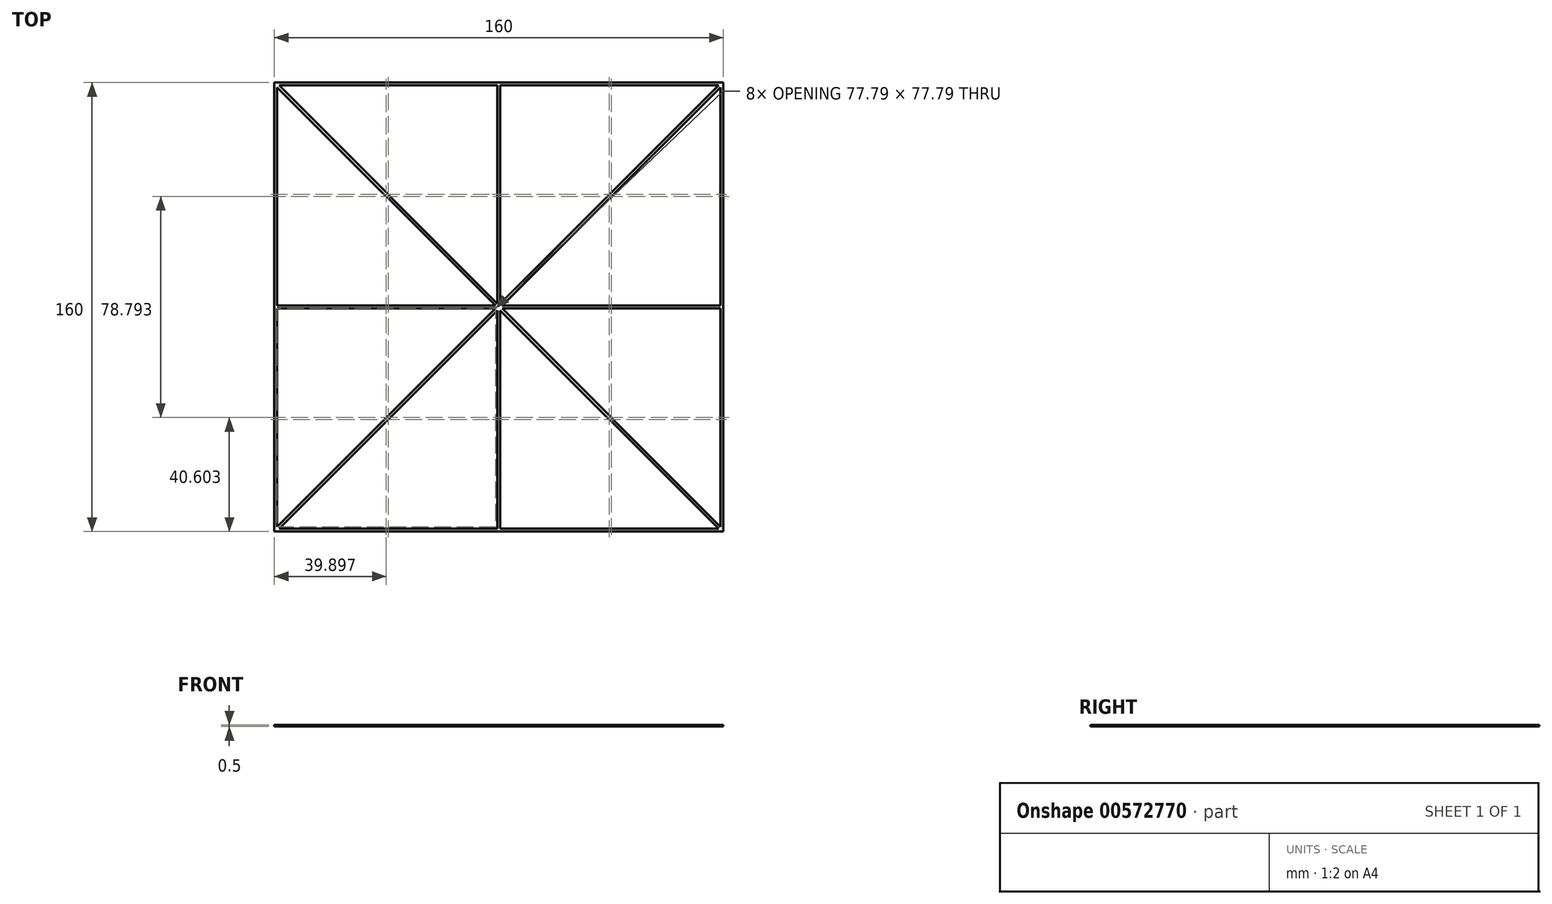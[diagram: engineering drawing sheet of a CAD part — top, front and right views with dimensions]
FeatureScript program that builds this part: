
annotation { "Feature Type Name" : "Feature", "Feature Type Description" : "" }
export const myFeature = defineFeature(function(context is Context, id is Id, definition is map)
    precondition{}
    {
        {
            var Q0;
            Q0=qCreatedBy(makeId("Top.planeOp"),FACE);
            var sketch = newSketch(context, id + "F0", { "sketchPlane" : qUnion([Q0])});
            skLineSegment(sketch, "E0.bottom", {"start": v(0, 0) * mm, "end": v(160, 0) * mm});
            skLineSegment(sketch, "E0.top", {"start": v(0, -160) * mm, "end": v(160, -160) * mm});
            skLineSegment(sketch, "E0.left", {"start": v(0, 0) * mm, "end": v(0, -160) * mm});
            skLineSegment(sketch, "E0.right", {"start": v(160, 0) * mm, "end": v(160, -160) * mm});
            skLineSegment(sketch, "E1", {"start": v(0, 0) * mm, "end": v(0, -1) * mm});
            skLineSegment(sketch, "E2", {"start": v(0, -1) * mm, "end": v(1, -1) * mm});
            skLineSegment(sketch, "E3.bottom", {"start": v(1, -1) * mm, "end": v(159, -1) * mm});
            skLineSegment(sketch, "E3.top", {"start": v(1, -159) * mm, "end": v(159, -159) * mm});
            skLineSegment(sketch, "E3.left", {"start": v(1, -1) * mm, "end": v(1, -159) * mm});
            skLineSegment(sketch, "E3.right", {"start": v(159, -1) * mm, "end": v(159, -159) * mm});
            skLineSegment(sketch, "E4", {"start": v(1, -80) * mm, "end": v(1, -79.5) * mm});
            skLineSegment(sketch, "E5", {"start": v(1, -79.5) * mm, "end": v(159, -79.5) * mm});
            skLineSegment(sketch, "E6", {"start": v(159, -79.5) * mm, "end": v(159, -80.5) * mm});
            skLineSegment(sketch, "E7", {"start": v(159, -80.5) * mm, "end": v(1, -80.5) * mm});
            skLineSegment(sketch, "E8", {"start": v(1, -80.5) * mm, "end": v(1, -79.5) * mm});
            skLineSegment(sketch, "E9", {"start": v(80, -159) * mm, "end": v(80.5, -159) * mm});
            skLineSegment(sketch, "E10", {"start": v(80.5, -159) * mm, "end": v(80.5, -1) * mm});
            skLineSegment(sketch, "E11", {"start": v(80.5, -1) * mm, "end": v(80, -1) * mm});
            skLineSegment(sketch, "E12", {"start": v(80, -1) * mm, "end": v(80, -159) * mm});
            skLineSegment(sketch, "E13", {"start": v(1, -159) * mm, "end": v(159, -1) * mm});
            skLineSegment(sketch, "E14", {"start": v(150.15, -9.85) * mm, "end": v(150.5, -10.2) * mm});
            skLineSegment(sketch, "E15", {"start": v(150.5, -10.2) * mm, "end": v(149.8, -9.5) * mm});
            skLineSegment(sketch, "E16", {"start": v(149.8, -9.5) * mm, "end": v(158.3, -1) * mm});
            skLineSegment(sketch, "E17", {"start": v(158.3, -1) * mm, "end": v(1, -158.3) * mm});
            skLineSegment(sketch, "E18", {"start": v(1, -158.3) * mm, "end": v(1.7, -159) * mm});
            skLineSegment(sketch, "E19", {"start": v(1.7, -159) * mm, "end": v(159, -1.7) * mm});
            skLineSegment(sketch, "E20", {"start": v(1, -1) * mm, "end": v(159, -159) * mm});
            skLineSegment(sketch, "E21", {"start": v(146.24, -146.24) * mm, "end": v(146.6, -145.89) * mm});
            skLineSegment(sketch, "E22", {"start": v(146.6, -145.89) * mm, "end": v(145.89, -146.6) * mm});
            skLineSegment(sketch, "E23", {"start": v(145.89, -146.6) * mm, "end": v(158.3, -159) * mm});
            skLineSegment(sketch, "E24", {"start": v(158.3, -159) * mm, "end": v(159, -158.3) * mm});
            skLineSegment(sketch, "E25", {"start": v(159, -158.3) * mm, "end": v(1.7, -1) * mm});
            skLineSegment(sketch, "E26", {"start": v(1.7, -1) * mm, "end": v(1, -1.7) * mm});
            skLineSegment(sketch, "E27", {"start": v(1, -1.7) * mm, "end": v(158.3, -159) * mm});
            skLineSegment(sketch, "E28", {"start": v(80, -1) * mm, "end": v(79.5, -1) * mm});
            skLineSegment(sketch, "E29", {"start": v(79.5, -1) * mm, "end": v(79.5, -159) * mm});
            skSolve(sketch);
        }
        {
            var Q0;
            {var subQ0=sQuery(id+"F0.wireOp",EDGE,"E12");var subQ1=sQuery(id+"F0.wireOp",EDGE,"E7");var subQ2=makeQuery(id+"F0.imprint","INTERSECT",VERTEX,{"derivedFrom":[subQ1,subQ0]});Q0=makeQuery(id+"F0.imprint","IMPRINT",FACE,{"disambiguationData":[TD([[makeQuery(id+"F0.imprint","IMPRINT",EDGE,{"disambiguationData":[TD([[subQ2,1.0]])],"derivedFrom":subQ1}),1.0]])]});}
            var Q1;
            {var subQ0=sQuery(id+"F0.wireOp",EDGE,"E12");var subQ1=sQuery(id+"F0.wireOp",EDGE,"E7");var subQ2=makeQuery(id+"F0.imprint","INTERSECT",VERTEX,{"derivedFrom":[subQ1,subQ0]});Q1=makeQuery(id+"F0.imprint","IMPRINT",FACE,{"disambiguationData":[TD([[makeQuery(id+"F0.imprint","IMPRINT",EDGE,{"disambiguationData":[TD([[subQ2,-1.0]])],"derivedFrom":subQ1}),1.0]])]});}
            var Q2;
            {var subQ31=sQuery(id+"F0.wireOp",EDGE,"E0.bottom");Q2=makeQuery(id+"F0.imprint","IMPRINT",FACE,{"disambiguationData":[TD([[makeQuery(id+"F0.imprint","IMPRINT",EDGE,{"derivedFrom":subQ31}),-1.0]])]});}
            var Q3;
            {var subQ0=sQuery(id+"F0.wireOp",EDGE,"E20");var subQ3=sQuery(id+"F0.wireOp",EDGE,"E26");var subQ5=makeQuery(id+"F0.imprint","INTERSECT",VERTEX,{"derivedFrom":[subQ0,subQ3]});Q3=makeQuery(id+"F0.imprint","IMPRINT",FACE,{"disambiguationData":[TD([[makeQuery(id+"F0.imprint","IMPRINT",EDGE,{"disambiguationData":[TD([[subQ5,1.0]])],"derivedFrom":subQ0}),1.0]])]});}
            var Q4;
            {var subQ0=sQuery(id+"F0.wireOp",EDGE,"E12");var subQ1=sQuery(id+"F0.wireOp",EDGE,"E3.bottom");var subQ2=makeQuery(id+"F0.imprint","INTERSECT",VERTEX,{"derivedFrom":[subQ1,subQ0]});Q4=makeQuery(id+"F0.imprint","IMPRINT",FACE,{"disambiguationData":[TD([[makeQuery(id+"F0.imprint","IMPRINT",EDGE,{"disambiguationData":[TD([[subQ2,-1.0]])],"derivedFrom":subQ1}),-1.0]])]});}
            var Q5;
            {var subQ1=sQuery(id+"F0.wireOp",EDGE,"E5");var subQ6=sQuery(id+"F0.wireOp",EDGE,"E3.right");var subQ9=makeQuery(id+"F0.imprint","INTERSECT",VERTEX,{"derivedFrom":[subQ6,subQ1]});Q5=makeQuery(id+"F0.imprint","IMPRINT",FACE,{"disambiguationData":[TD([[makeQuery(id+"F0.imprint","IMPRINT",EDGE,{"disambiguationData":[TD([[subQ9,-1.0]])],"derivedFrom":subQ6}),-1.0]])]});}
            var Q6;
            {var subQ0=sQuery(id+"F0.wireOp",EDGE,"E18");var subQ3=sQuery(id+"F0.wireOp",EDGE,"E13");var subQ5=makeQuery(id+"F0.imprint","INTERSECT",VERTEX,{"derivedFrom":[subQ3,subQ0]});Q6=makeQuery(id+"F0.imprint","IMPRINT",FACE,{"disambiguationData":[TD([[makeQuery(id+"F0.imprint","IMPRINT",EDGE,{"disambiguationData":[TD([[subQ5,1.0]])],"derivedFrom":subQ3}),-1.0]])]});}
            var Q7;
            {var subQ1=sQuery(id+"F0.wireOp",EDGE,"E3.left");var subQ5=makeQuery(id+"F0.imprint","IMPRINT",VERTEX,{"derivedFrom":subQ1});Q7=makeQuery(id+"F0.imprint","IMPRINT",FACE,{"disambiguationData":[TD([[makeQuery(id+"F0.imprint","IMPRINT",EDGE,{"disambiguationData":[TD([[subQ5,-1.0]])],"derivedFrom":subQ1}),1.0]])]});}
            var Q8;
            {var subQ0=sQuery(id+"F0.wireOp",EDGE,"E25");var subQ1=sQuery(id+"F0.wireOp",EDGE,"E5");var subQ2=makeQuery(id+"F0.imprint","INTERSECT",VERTEX,{"derivedFrom":[subQ1,subQ0]});Q8=makeQuery(id+"F0.imprint","IMPRINT",FACE,{"disambiguationData":[TD([[makeQuery(id+"F0.imprint","IMPRINT",EDGE,{"disambiguationData":[TD([[subQ2,1.0]])],"derivedFrom":subQ0}),-1.0]])]});}
            var Q9;
            {var subQ0=sQuery(id+"F0.wireOp",EDGE,"E12");var subQ1=sQuery(id+"F0.wireOp",EDGE,"E7");var subQ2=makeQuery(id+"F0.imprint","INTERSECT",VERTEX,{"derivedFrom":[subQ1,subQ0]});Q9=makeQuery(id+"F0.imprint","IMPRINT",FACE,{"disambiguationData":[TD([[makeQuery(id+"F0.imprint","IMPRINT",EDGE,{"disambiguationData":[TD([[subQ2,-1.0]])],"derivedFrom":subQ1}),-1.0]])]});}
            var Q10;
            {var subQ0=sQuery(id+"F0.wireOp",EDGE,"E25");var subQ1=sQuery(id+"F0.wireOp",EDGE,"E5");var subQ2=makeQuery(id+"F0.imprint","INTERSECT",VERTEX,{"derivedFrom":[subQ1,subQ0]});Q10=makeQuery(id+"F0.imprint","IMPRINT",FACE,{"disambiguationData":[TD([[makeQuery(id+"F0.imprint","IMPRINT",EDGE,{"disambiguationData":[TD([[subQ2,1.0]])],"derivedFrom":subQ1}),-1.0]])]});}
            var Q11;
            {var subQ0=sQuery(id+"F0.wireOp",EDGE,"E25");var subQ1=sQuery(id+"F0.wireOp",EDGE,"E5");var subQ2=makeQuery(id+"F0.imprint","INTERSECT",VERTEX,{"derivedFrom":[subQ1,subQ0]});Q11=makeQuery(id+"F0.imprint","IMPRINT",FACE,{"disambiguationData":[TD([[makeQuery(id+"F0.imprint","IMPRINT",EDGE,{"disambiguationData":[TD([[subQ2,1.0]])],"derivedFrom":subQ1}),1.0]])]});}
            var Q12;
            {var subQ0=sQuery(id+"F0.wireOp",EDGE,"E12");var subQ1=sQuery(id+"F0.wireOp",EDGE,"E5");var subQ2=makeQuery(id+"F0.imprint","INTERSECT",VERTEX,{"derivedFrom":[subQ1,subQ0]});Q12=makeQuery(id+"F0.imprint","IMPRINT",FACE,{"disambiguationData":[TD([[makeQuery(id+"F0.imprint","IMPRINT",EDGE,{"disambiguationData":[TD([[subQ2,1.0]])],"derivedFrom":subQ1}),1.0]])]});}
            var Q13;
            {var subQ0=sQuery(id+"F0.wireOp",EDGE,"E19");var subQ1=sQuery(id+"F0.wireOp",EDGE,"E5");var subQ2=makeQuery(id+"F0.imprint","INTERSECT",VERTEX,{"derivedFrom":[subQ1,subQ0]});Q13=makeQuery(id+"F0.imprint","IMPRINT",FACE,{"disambiguationData":[TD([[makeQuery(id+"F0.imprint","IMPRINT",EDGE,{"disambiguationData":[TD([[subQ2,1.0]])],"derivedFrom":subQ0}),1.0]])]});}
            var Q14;
            {var subQ0=sQuery(id+"F0.wireOp",EDGE,"E19");var subQ1=sQuery(id+"F0.wireOp",EDGE,"E10");var subQ2=makeQuery(id+"F0.imprint","INTERSECT",VERTEX,{"derivedFrom":[subQ1,subQ0]});Q14=makeQuery(id+"F0.imprint","IMPRINT",FACE,{"disambiguationData":[TD([[makeQuery(id+"F0.imprint","IMPRINT",EDGE,{"disambiguationData":[TD([[subQ2,-1.0]])],"derivedFrom":subQ1}),-1.0]])]});}
            var Q15;
            {var subQ0=sQuery(id+"F0.wireOp",EDGE,"E13");var subQ3=sQuery(id+"F0.wireOp",EDGE,"E27");var subQ5=makeQuery(id+"F0.imprint","INTERSECT",VERTEX,{"derivedFrom":[subQ0,subQ3]});Q15=makeQuery(id+"F0.imprint","IMPRINT",FACE,{"disambiguationData":[TD([[makeQuery(id+"F0.imprint","IMPRINT",EDGE,{"disambiguationData":[TD([[subQ5,-1.0]])],"derivedFrom":subQ3}),-1.0]])]});}
            var Q16;
            {var subQ0=sQuery(id+"F0.wireOp",EDGE,"E19");var subQ1=sQuery(id+"F0.wireOp",EDGE,"E7");var subQ2=makeQuery(id+"F0.imprint","INTERSECT",VERTEX,{"derivedFrom":[subQ1,subQ0]});Q16=makeQuery(id+"F0.imprint","IMPRINT",FACE,{"disambiguationData":[TD([[makeQuery(id+"F0.imprint","IMPRINT",EDGE,{"disambiguationData":[TD([[subQ2,-1.0]])],"derivedFrom":subQ0}),-1.0]])]});}
            var Q17;
            {var subQ0=sQuery(id+"F0.wireOp",EDGE,"E19");var subQ1=sQuery(id+"F0.wireOp",EDGE,"E7");var subQ2=makeQuery(id+"F0.imprint","INTERSECT",VERTEX,{"derivedFrom":[subQ1,subQ0]});Q17=makeQuery(id+"F0.imprint","IMPRINT",FACE,{"disambiguationData":[TD([[makeQuery(id+"F0.imprint","IMPRINT",EDGE,{"disambiguationData":[TD([[subQ2,1.0]])],"derivedFrom":subQ1}),1.0]])]});}
            var Q18;
            {var subQ0=sQuery(id+"F0.wireOp",EDGE,"E12");var subQ1=sQuery(id+"F0.wireOp",EDGE,"E3.bottom");var subQ2=makeQuery(id+"F0.imprint","INTERSECT",VERTEX,{"derivedFrom":[subQ1,subQ0]});Q18=makeQuery(id+"F0.imprint","IMPRINT",FACE,{"disambiguationData":[TD([[makeQuery(id+"F0.imprint","IMPRINT",EDGE,{"disambiguationData":[TD([[subQ2,1.0]])],"derivedFrom":subQ1}),-1.0]])]});}
            var Q19;
            {var subQ0=sQuery(id+"F0.wireOp",EDGE,"E26");var subQ1=sQuery(id+"F0.wireOp",EDGE,"E20");var subQ2=makeQuery(id+"F0.imprint","INTERSECT",VERTEX,{"derivedFrom":[subQ1,subQ0]});Q19=makeQuery(id+"F0.imprint","IMPRINT",FACE,{"disambiguationData":[TD([[makeQuery(id+"F0.imprint","IMPRINT",EDGE,{"disambiguationData":[TD([[subQ2,-1.0]])],"derivedFrom":subQ1}),1.0]])]});}
            var Q20;
            {var subQ0=sQuery(id+"F0.wireOp",EDGE,"E27");var subQ1=sQuery(id+"F0.wireOp",EDGE,"E5");var subQ2=makeQuery(id+"F0.imprint","INTERSECT",VERTEX,{"derivedFrom":[subQ1,subQ0]});Q20=makeQuery(id+"F0.imprint","IMPRINT",FACE,{"disambiguationData":[TD([[makeQuery(id+"F0.imprint","IMPRINT",EDGE,{"disambiguationData":[TD([[subQ2,-1.0]])],"derivedFrom":subQ1}),1.0]])]});}
            var Q21;
            {var subQ5=sQuery(id+"F0.wireOp",EDGE,"E15");Q21=makeQuery(id+"F0.imprint","IMPRINT",FACE,{"disambiguationData":[TD([[makeQuery(id+"F0.imprint","IMPRINT",EDGE,{"derivedFrom":subQ5}),1.0]])]});}
            var Q22;
            {var subQ5=sQuery(id+"F0.wireOp",EDGE,"E21");Q22=makeQuery(id+"F0.imprint","IMPRINT",FACE,{"disambiguationData":[TD([[makeQuery(id+"F0.imprint","IMPRINT",EDGE,{"derivedFrom":subQ5}),1.0]])]});}
            var Q23;
            {var subQ5=sQuery(id+"F0.wireOp",EDGE,"E22");Q23=makeQuery(id+"F0.imprint","IMPRINT",FACE,{"disambiguationData":[TD([[makeQuery(id+"F0.imprint","IMPRINT",EDGE,{"derivedFrom":subQ5}),-1.0]])]});}
            var Q24;
            {var subQ0=sQuery(id+"F0.wireOp",EDGE,"E10");var subQ1=sQuery(id+"F0.wireOp",EDGE,"E3.top");var subQ2=makeQuery(id+"F0.imprint","INTERSECT",VERTEX,{"derivedFrom":[subQ1,subQ0]});Q24=makeQuery(id+"F0.imprint","IMPRINT",FACE,{"disambiguationData":[TD([[makeQuery(id+"F0.imprint","IMPRINT",EDGE,{"disambiguationData":[TD([[subQ2,1.0]])],"derivedFrom":subQ1}),1.0]])]});}
            var Q25;
            {var subQ0=sQuery(id+"F0.wireOp",EDGE,"E29");var subQ1=sQuery(id+"F0.wireOp",EDGE,"E3.top");var subQ2=makeQuery(id+"F0.imprint","INTERSECT",VERTEX,{"derivedFrom":[subQ1,subQ0]});Q25=makeQuery(id+"F0.imprint","IMPRINT",FACE,{"disambiguationData":[TD([[makeQuery(id+"F0.imprint","IMPRINT",EDGE,{"disambiguationData":[TD([[subQ2,-1.0]])],"derivedFrom":subQ1}),1.0]])]});}
            var Q26;
            {var subQ0=sQuery(id+"F0.wireOp",EDGE,"E18");var subQ1=sQuery(id+"F0.wireOp",EDGE,"E13");var subQ2=makeQuery(id+"F0.imprint","INTERSECT",VERTEX,{"derivedFrom":[subQ1,subQ0]});Q26=makeQuery(id+"F0.imprint","IMPRINT",FACE,{"disambiguationData":[TD([[makeQuery(id+"F0.imprint","IMPRINT",EDGE,{"disambiguationData":[TD([[subQ2,-1.0]])],"derivedFrom":subQ1}),-1.0]])]});}
            var Q27;
            {var subQ0=sQuery(id+"F0.wireOp",EDGE,"E17");var subQ1=sQuery(id+"F0.wireOp",EDGE,"E7");var subQ2=makeQuery(id+"F0.imprint","INTERSECT",VERTEX,{"derivedFrom":[subQ1,subQ0]});Q27=makeQuery(id+"F0.imprint","IMPRINT",FACE,{"disambiguationData":[TD([[makeQuery(id+"F0.imprint","IMPRINT",EDGE,{"disambiguationData":[TD([[subQ2,1.0]])],"derivedFrom":subQ1}),1.0]])]});}
            var Q28;
            {var subQ3=sQuery(id+"F0.wireOp",EDGE,"E10");var subQ5=sQuery(id+"F0.wireOp",EDGE,"E19");var subQ6=makeQuery(id+"F0.imprint","INTERSECT",VERTEX,{"derivedFrom":[subQ3,subQ5]});Q28=makeQuery(id+"F0.imprint","IMPRINT",FACE,{"disambiguationData":[TD([[makeQuery(id+"F0.imprint","IMPRINT",EDGE,{"disambiguationData":[TD([[subQ6,-1.0]])],"derivedFrom":subQ5}),-1.0]])]});}
            var Q29;
            {var subQ1=sQuery(id+"F0.wireOp",EDGE,"E7");var subQ3=sQuery(id+"F0.wireOp",EDGE,"E27");var subQ4=makeQuery(id+"F0.imprint","INTERSECT",VERTEX,{"derivedFrom":[subQ1,subQ3]});Q29=makeQuery(id+"F0.imprint","IMPRINT",FACE,{"disambiguationData":[TD([[makeQuery(id+"F0.imprint","IMPRINT",EDGE,{"disambiguationData":[TD([[subQ4,-1.0]])],"derivedFrom":subQ1}),1.0]])]});}
            var Q30;
            {var subQ0=sQuery(id+"F0.wireOp",EDGE,"E17");var subQ1=sQuery(id+"F0.wireOp",EDGE,"E7");var subQ2=makeQuery(id+"F0.imprint","INTERSECT",VERTEX,{"derivedFrom":[subQ1,subQ0]});Q30=makeQuery(id+"F0.imprint","IMPRINT",FACE,{"disambiguationData":[TD([[makeQuery(id+"F0.imprint","IMPRINT",EDGE,{"disambiguationData":[TD([[subQ2,1.0]])],"derivedFrom":subQ0}),1.0]])]});}
            var Q31;
            {var subQ0=sQuery(id+"F0.wireOp",EDGE,"E25");var subQ1=sQuery(id+"F0.wireOp",EDGE,"E5");var subQ2=makeQuery(id+"F0.imprint","INTERSECT",VERTEX,{"derivedFrom":[subQ1,subQ0]});Q31=makeQuery(id+"F0.imprint","IMPRINT",FACE,{"disambiguationData":[TD([[makeQuery(id+"F0.imprint","IMPRINT",EDGE,{"disambiguationData":[TD([[subQ2,-1.0]])],"derivedFrom":subQ1}),1.0]])]});}
            var Q32;
            {var subQ0=sQuery(id+"F0.wireOp",EDGE,"E17");var subQ1=sQuery(id+"F0.wireOp",EDGE,"E5");var subQ2=makeQuery(id+"F0.imprint","INTERSECT",VERTEX,{"derivedFrom":[subQ1,subQ0]});Q32=makeQuery(id+"F0.imprint","IMPRINT",FACE,{"disambiguationData":[TD([[makeQuery(id+"F0.imprint","IMPRINT",EDGE,{"disambiguationData":[TD([[subQ2,1.0]])],"derivedFrom":subQ1}),1.0]])]});}
            var Q33;
            {var subQ3=sQuery(id+"F0.wireOp",EDGE,"E29");var subQ5=sQuery(id+"F0.wireOp",EDGE,"E17");var subQ7=makeQuery(id+"F0.imprint","INTERSECT",VERTEX,{"derivedFrom":[subQ5,subQ3]});Q33=makeQuery(id+"F0.imprint","IMPRINT",FACE,{"disambiguationData":[TD([[makeQuery(id+"F0.imprint","IMPRINT",EDGE,{"disambiguationData":[TD([[subQ7,-1.0]])],"derivedFrom":subQ5}),-1.0]])]});}
            var Q34;
            {var subQ3=sQuery(id+"F0.wireOp",EDGE,"E29");var subQ5=sQuery(id+"F0.wireOp",EDGE,"E17");var subQ6=makeQuery(id+"F0.imprint","INTERSECT",VERTEX,{"derivedFrom":[subQ5,subQ3]});Q34=makeQuery(id+"F0.imprint","IMPRINT",FACE,{"disambiguationData":[TD([[makeQuery(id+"F0.imprint","IMPRINT",EDGE,{"disambiguationData":[TD([[subQ6,1.0]])],"derivedFrom":subQ5}),1.0]])]});}
            var Q35;
            {var subQ0=sQuery(id+"F0.wireOp",EDGE,"E12");var subQ1=sQuery(id+"F0.wireOp",EDGE,"E5");var subQ2=makeQuery(id+"F0.imprint","INTERSECT",VERTEX,{"derivedFrom":[subQ1,subQ0]});Q35=makeQuery(id+"F0.imprint","IMPRINT",FACE,{"disambiguationData":[TD([[makeQuery(id+"F0.imprint","IMPRINT",EDGE,{"disambiguationData":[TD([[subQ2,1.0]])],"derivedFrom":subQ1}),-1.0]])]});}
            var Q36;
            {var subQ0=sQuery(id+"F0.wireOp",EDGE,"E12");var subQ1=sQuery(id+"F0.wireOp",EDGE,"E7");var subQ2=makeQuery(id+"F0.imprint","INTERSECT",VERTEX,{"derivedFrom":[subQ1,subQ0]});Q36=makeQuery(id+"F0.imprint","IMPRINT",FACE,{"disambiguationData":[TD([[makeQuery(id+"F0.imprint","IMPRINT",EDGE,{"disambiguationData":[TD([[subQ2,1.0]])],"derivedFrom":subQ1}),-1.0]])]});}
            var Q37;
            {var subQ0=sQuery(id+"F0.wireOp",EDGE,"E19");var subQ1=sQuery(id+"F0.wireOp",EDGE,"E10");var subQ2=makeQuery(id+"F0.imprint","INTERSECT",VERTEX,{"derivedFrom":[subQ1,subQ0]});Q37=makeQuery(id+"F0.imprint","IMPRINT",FACE,{"disambiguationData":[TD([[makeQuery(id+"F0.imprint","IMPRINT",EDGE,{"disambiguationData":[TD([[subQ2,-1.0]])],"derivedFrom":subQ1}),1.0]])]});}
            var Q38;
            {var subQ0=sQuery(id+"F0.wireOp",EDGE,"E19");var subQ1=sQuery(id+"F0.wireOp",EDGE,"E10");var subQ2=makeQuery(id+"F0.imprint","INTERSECT",VERTEX,{"derivedFrom":[subQ1,subQ0]});Q38=makeQuery(id+"F0.imprint","IMPRINT",FACE,{"disambiguationData":[TD([[makeQuery(id+"F0.imprint","IMPRINT",EDGE,{"disambiguationData":[TD([[subQ2,1.0]])],"derivedFrom":subQ0}),-1.0]])]});}
            var Q39;
            {var subQ1=sQuery(id+"F0.wireOp",EDGE,"E10");var subQ3=sQuery(id+"F0.wireOp",EDGE,"E25");var subQ4=makeQuery(id+"F0.imprint","INTERSECT",VERTEX,{"derivedFrom":[subQ1,subQ3]});Q39=makeQuery(id+"F0.imprint","IMPRINT",FACE,{"disambiguationData":[TD([[makeQuery(id+"F0.imprint","IMPRINT",EDGE,{"disambiguationData":[TD([[subQ4,-1.0]])],"derivedFrom":subQ3}),-1.0]])]});}
            var Q40;
            {var subQ5=sQuery(id+"F0.wireOp",EDGE,"E14");Q40=makeQuery(id+"F0.imprint","IMPRINT",FACE,{"disambiguationData":[TD([[makeQuery(id+"F0.imprint","IMPRINT",EDGE,{"derivedFrom":subQ5}),-1.0]])]});}
            var Q41;
            {var subQ0=sQuery(id+"F0.wireOp",EDGE,"E29");var subQ1=sQuery(id+"F0.wireOp",EDGE,"E17");var subQ2=makeQuery(id+"F0.imprint","INTERSECT",VERTEX,{"derivedFrom":[subQ1,subQ0]});Q41=makeQuery(id+"F0.imprint","IMPRINT",FACE,{"disambiguationData":[TD([[makeQuery(id+"F0.imprint","IMPRINT",EDGE,{"disambiguationData":[TD([[subQ2,-1.0]])],"derivedFrom":subQ1}),1.0]])]});}
            var Q42;
            {var subQ0=sQuery(id+"F0.wireOp",EDGE,"E29");var subQ1=sQuery(id+"F0.wireOp",EDGE,"E17");var subQ2=makeQuery(id+"F0.imprint","INTERSECT",VERTEX,{"derivedFrom":[subQ1,subQ0]});Q42=makeQuery(id+"F0.imprint","IMPRINT",FACE,{"disambiguationData":[TD([[makeQuery(id+"F0.imprint","IMPRINT",EDGE,{"disambiguationData":[TD([[subQ2,1.0]])],"derivedFrom":subQ1}),-1.0]])]});}
            var Q43;
            {var subQ0=sQuery(id+"F0.wireOp",EDGE,"E17");var subQ3=sQuery(id+"F0.wireOp",EDGE,"E20");var subQ5=makeQuery(id+"F0.imprint","INTERSECT",VERTEX,{"derivedFrom":[subQ0,subQ3]});Q43=makeQuery(id+"F0.imprint","IMPRINT",FACE,{"disambiguationData":[TD([[makeQuery(id+"F0.imprint","IMPRINT",EDGE,{"disambiguationData":[TD([[subQ5,1.0]])],"derivedFrom":subQ0}),-1.0]])]});}
            var Q44;
            {var subQ0=sQuery(id+"F0.wireOp",EDGE,"E27");var subQ1=sQuery(id+"F0.wireOp",EDGE,"E13");var subQ2=makeQuery(id+"F0.imprint","INTERSECT",VERTEX,{"derivedFrom":[subQ1,subQ0]});Q44=makeQuery(id+"F0.imprint","IMPRINT",FACE,{"disambiguationData":[TD([[makeQuery(id+"F0.imprint","IMPRINT",EDGE,{"disambiguationData":[TD([[subQ2,1.0]])],"derivedFrom":subQ0}),-1.0]])]});}
            var Q45;
            {var subQ0=sQuery(id+"F0.wireOp",EDGE,"E20");var subQ3=sQuery(id+"F0.wireOp",EDGE,"E26");var subQ5=makeQuery(id+"F0.imprint","INTERSECT",VERTEX,{"derivedFrom":[subQ0,subQ3]});Q45=makeQuery(id+"F0.imprint","IMPRINT",FACE,{"disambiguationData":[TD([[makeQuery(id+"F0.imprint","IMPRINT",EDGE,{"disambiguationData":[TD([[subQ5,1.0]])],"derivedFrom":subQ0}),-1.0]])]});}
            var Q46;
            {var subQ5=sQuery(id+"F0.wireOp",EDGE,"E14");Q46=makeQuery(id+"F0.imprint","IMPRINT",FACE,{"disambiguationData":[TD([[makeQuery(id+"F0.imprint","IMPRINT",EDGE,{"derivedFrom":subQ5}),1.0]])]});}
            var Q47;
            {var subQ4=sQuery(id+"F0.wireOp",EDGE,"E15");Q47=makeQuery(id+"F0.imprint","IMPRINT",FACE,{"disambiguationData":[TD([[makeQuery(id+"F0.imprint","IMPRINT",EDGE,{"derivedFrom":subQ4}),-1.0]])]});}
            var Q48;
            {var subQ0=sQuery(id+"F0.wireOp",EDGE,"E21");Q48=makeQuery(id+"F0.imprint","IMPRINT",FACE,{"disambiguationData":[TD([[makeQuery(id+"F0.imprint","IMPRINT",EDGE,{"derivedFrom":subQ0}),-1.0]])]});}
            var Q49;
            {var subQ0=sQuery(id+"F0.wireOp",EDGE,"E22");Q49=makeQuery(id+"F0.imprint","IMPRINT",FACE,{"disambiguationData":[TD([[makeQuery(id+"F0.imprint","IMPRINT",EDGE,{"derivedFrom":subQ0}),1.0]])]});}
            var Q50;
            {var subQ0=sQuery(id+"F0.wireOp",EDGE,"E24");var subQ3=sQuery(id+"F0.wireOp",EDGE,"E20");var subQ5=makeQuery(id+"F0.imprint","INTERSECT",VERTEX,{"derivedFrom":[subQ3,subQ0]});Q50=makeQuery(id+"F0.imprint","IMPRINT",FACE,{"disambiguationData":[TD([[makeQuery(id+"F0.imprint","IMPRINT",EDGE,{"disambiguationData":[TD([[subQ5,-1.0]])],"derivedFrom":subQ3}),-1.0]])]});}
            var Q51;
            {var subQ0=sQuery(id+"F0.wireOp",EDGE,"E20");var subQ3=sQuery(id+"F0.wireOp",EDGE,"E24");var subQ5=makeQuery(id+"F0.imprint","INTERSECT",VERTEX,{"derivedFrom":[subQ0,subQ3]});Q51=makeQuery(id+"F0.imprint","IMPRINT",FACE,{"disambiguationData":[TD([[makeQuery(id+"F0.imprint","IMPRINT",EDGE,{"disambiguationData":[TD([[subQ5,-1.0]])],"derivedFrom":subQ0}),1.0]])]});}
            var Q52;
            {var subQ0=sQuery(id+"F0.wireOp",EDGE,"E13");var subQ3=sQuery(id+"F0.wireOp",EDGE,"E18");var subQ5=makeQuery(id+"F0.imprint","INTERSECT",VERTEX,{"derivedFrom":[subQ0,subQ3]});Q52=makeQuery(id+"F0.imprint","IMPRINT",FACE,{"disambiguationData":[TD([[makeQuery(id+"F0.imprint","IMPRINT",EDGE,{"disambiguationData":[TD([[subQ5,1.0]])],"derivedFrom":subQ0}),1.0]])]});}
            extrude(context, id + "F1", {"entities" : qUnion([Q0, Q1, Q2, Q3, Q4, Q5, Q6, Q7, Q8, Q9, Q10, Q11, Q12, Q13, Q14, Q15, Q16, Q17, Q18, Q19, Q20, Q21, Q22, Q23, Q24, Q25, Q26, Q27, Q28, Q29, Q30, Q31, Q32, Q33, Q34, Q35, Q36, Q37, Q38, Q39, Q40, Q41, Q42, Q43, Q44, Q45, Q46, Q47, Q48, Q49, Q50, Q51, Q52]), "depth" : 0.5 * mm, "offsetDistance" : 25 * mm});
        }
    });
